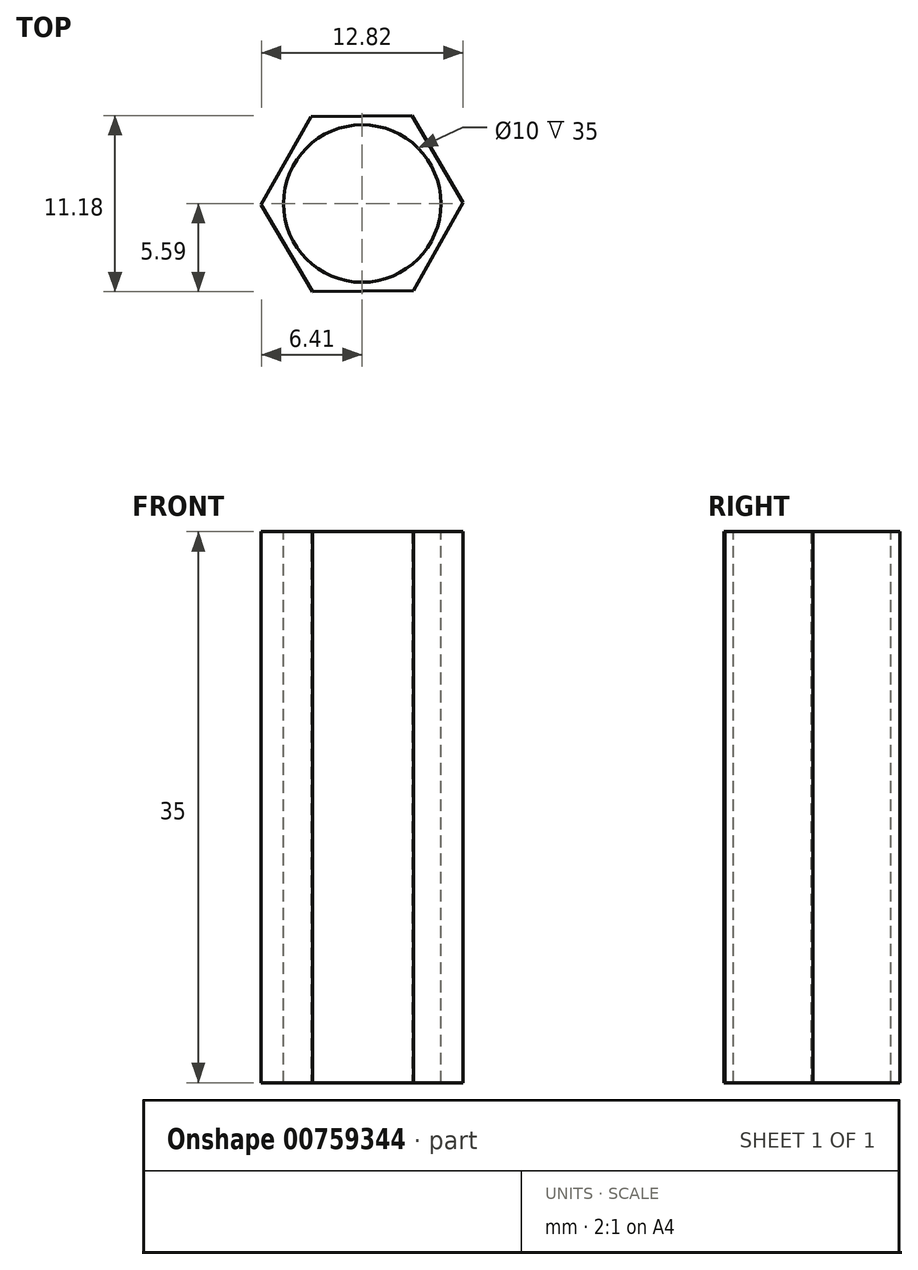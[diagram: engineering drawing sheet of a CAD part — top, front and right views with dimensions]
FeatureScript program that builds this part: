
annotation { "Feature Type Name" : "Feature", "Feature Type Description" : "" }
export const myFeature = defineFeature(function(context is Context, id is Id, definition is map)
    precondition{}
    {
        {
            var Q0;
            Q0=qCreatedBy(makeId("Top.planeOp"),FACE);
            var sketch = newSketch(context, id + "F0", { "sketchPlane" : qUnion([Q0])});
            skCircle(sketch, "E0.cCircle", {"center": v(0, 0) * mm, "radius": 5.55 * mm, "construction": true});
            skLineSegment(sketch, "E0.0", {"start": v(-6.41, -0.06) * mm, "end": v(-3.26, 5.52) * mm});
            skLineSegment(sketch, "E0.1", {"start": v(-3.26, 5.52) * mm, "end": v(3.15, 5.59) * mm});
            skLineSegment(sketch, "E0.2", {"start": v(3.15, 5.59) * mm, "end": v(6.41, 0.06) * mm});
            skLineSegment(sketch, "E0.3", {"start": v(6.41, 0.06) * mm, "end": v(3.26, -5.52) * mm});
            skLineSegment(sketch, "E0.4", {"start": v(3.26, -5.52) * mm, "end": v(-3.15, -5.59) * mm});
            skLineSegment(sketch, "E0.5", {"start": v(-3.15, -5.59) * mm, "end": v(-6.41, -0.06) * mm});
            skPoint(sketch, "E0.0.midPoint", {"position": v(-4.84, 2.73) * mm});
            skSolve(sketch);
        }
        {
            var Q0;
            Q0=makeQuery(id+"F0.imprint","IMPRINT",FACE,{"disambiguationData":[TD([[makeQuery(id+"F0.imprint","IMPRINT",EDGE,{"derivedFrom":sQuery(id+"F0.wireOp",EDGE,"E0.0")}),-1.0]])]});
            extrude(context, id + "F1", {"entities" : qUnion([Q0]), "depth" : 35 * mm, "offsetDistance" : 25 * mm});
        }
        {
            var Q0;
            Q0=makeQuery(id+"F1.opExtrude","CAP_FACE",FACE,{"disambiguationData":[OSD([sQuery(id+"F0.wireOp",EDGE,"E0.0"),sQuery(id+"F0.wireOp",EDGE,"E0.1"),sQuery(id+"F0.wireOp",EDGE,"E0.2"),sQuery(id+"F0.wireOp",EDGE,"E0.3"),sQuery(id+"F0.wireOp",EDGE,"E0.4"),sQuery(id+"F0.wireOp",EDGE,"E0.5")])],"isStart":false});
            var sketch = newSketch(context, id + "F2", { "sketchPlane" : qUnion([Q0])});
            skCircle(sketch, "E1", {"center": v(0, 0) * mm, "radius": 5 * mm});
            skSolve(sketch);
        }
        {
            var Q0;
            Q0=makeQuery(id+"F2.imprint","IMPRINT",FACE,{"disambiguationData":[TD([[makeQuery(id+"F2.imprint","IMPRINT",EDGE,{"derivedFrom":sQuery(id+"F2.wireOp",EDGE,"E1")}),1.0]])]});
            extrude(context, id + "F3", {"entities" : qUnion([Q0]), "operationType" : NewBodyOperationType.REMOVE, "oppositeDirection" : true, "depth" : 35 * mm, "offsetDistance" : 25 * mm});
        }
    });
